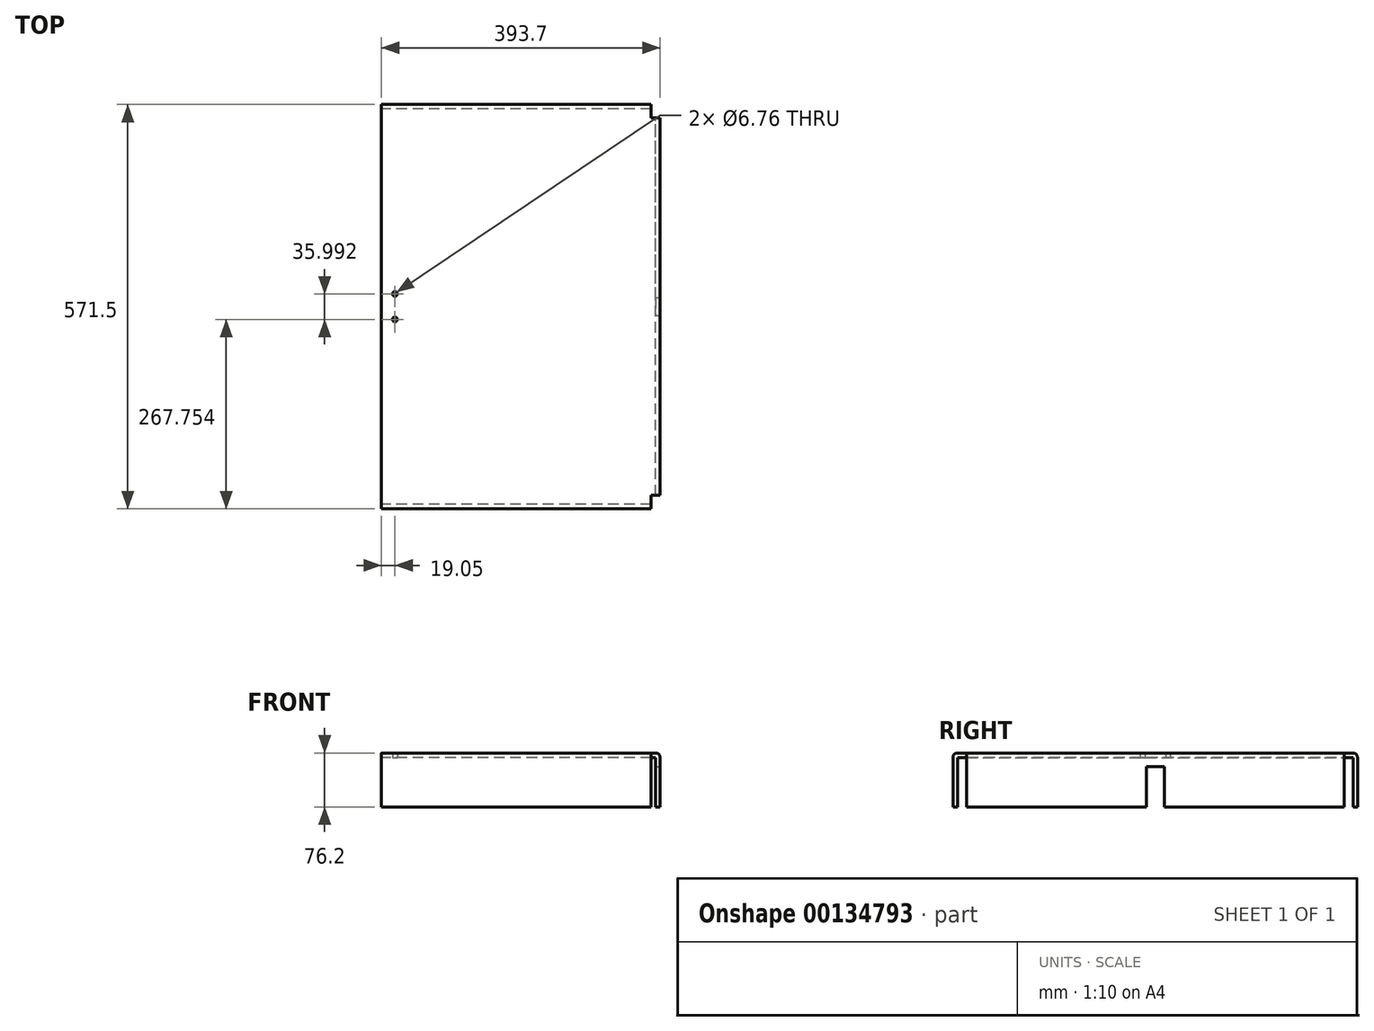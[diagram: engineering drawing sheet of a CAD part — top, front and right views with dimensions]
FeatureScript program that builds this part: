
annotation { "Feature Type Name" : "Feature", "Feature Type Description" : "" }
export const myFeature = defineFeature(function(context is Context, id is Id, definition is map)
    precondition{}
    {
        {
            var Q0;
            Q0=qCreatedBy(makeId("Top.planeOp"),FACE);
            var sketch = newSketch(context, id + "F0", { "sketchPlane" : qUnion([Q0])});
            skLineSegment(sketch, "E0.bottom", {"start": v(190.5, 279.4) * mm, "end": v(-190.5, 279.4) * mm});
            skLineSegment(sketch, "E0.top", {"start": v(190.5, -279.4) * mm, "end": v(-190.5, -279.4) * mm});
            skLineSegment(sketch, "E0.left", {"start": v(190.5, 279.4) * mm, "end": v(190.5, -279.4) * mm});
            skLineSegment(sketch, "E0.right", {"start": v(-190.5, 279.4) * mm, "end": v(-190.5, -279.4) * mm});
            skPoint(sketch, "E0.middle", {"position": v(0, 0) * mm});
            skSolve(sketch);
        }
        {
            var Q0;
            Q0=makeQuery(id+"F0.imprint","IMPRINT",FACE,{"disambiguationData":[TD([[makeQuery(id+"F0.imprint","IMPRINT",EDGE,{"derivedFrom":sQuery(id+"F0.wireOp",EDGE,"E0.bottom")}),1.0]])]});
            extrude(context, id + "F1", {"entities" : qUnion([Q0]), "depth" : 6.35 * mm});
        }
        {
            var Q0;
            Q0=makeQuery(id+"F1.opExtrude","CAP_FACE",FACE,{"disambiguationData":[OSD([sQuery(id+"F0.wireOp",EDGE,"E0.bottom"),sQuery(id+"F0.wireOp",EDGE,"E0.top"),sQuery(id+"F0.wireOp",EDGE,"E0.left"),sQuery(id+"F0.wireOp",EDGE,"E0.right")])],"isStart":false});
            var sketch = newSketch(context, id + "F2", { "sketchPlane" : qUnion([Q0])});
            skLineSegment(sketch, "E1.bottom", {"start": v(190.5, 279.4) * mm, "end": v(-190.5, 279.4) * mm});
            skLineSegment(sketch, "E1.top", {"start": v(190.5, 285.75) * mm, "end": v(-190.5, 285.75) * mm});
            skLineSegment(sketch, "E1.left", {"start": v(190.5, 279.4) * mm, "end": v(190.5, 285.75) * mm});
            skLineSegment(sketch, "E1.right", {"start": v(-190.5, 279.4) * mm, "end": v(-190.5, 285.75) * mm});
            skLineSegment(sketch, "E2.bottom", {"start": v(-190.5, -279.4) * mm, "end": v(190.5, -279.4) * mm});
            skLineSegment(sketch, "E2.top", {"start": v(-190.5, -285.75) * mm, "end": v(190.5, -285.75) * mm});
            skLineSegment(sketch, "E2.left", {"start": v(-190.5, -279.4) * mm, "end": v(-190.5, -285.75) * mm});
            skLineSegment(sketch, "E2.right", {"start": v(190.5, -279.4) * mm, "end": v(190.5, -285.75) * mm});
            skLineSegment(sketch, "E3.bottom", {"start": v(-190.5, -279.4) * mm, "end": v(-196.85, -279.4) * mm});
            skLineSegment(sketch, "E3.top", {"start": v(-190.5, 279.4) * mm, "end": v(-196.85, 279.4) * mm});
            skLineSegment(sketch, "E3.left", {"start": v(-190.5, -279.4) * mm, "end": v(-190.5, 279.4) * mm});
            skLineSegment(sketch, "E3.right", {"start": v(-196.85, -279.4) * mm, "end": v(-196.85, 279.4) * mm});
            skSolve(sketch);
        }
        {
            var Q0;
            Q0=makeQuery(id+"F2.imprint","IMPRINT",FACE,{"disambiguationData":[TD([[makeQuery(id+"F2.imprint","IMPRINT",EDGE,{"derivedFrom":sQuery(id+"F2.wireOp",EDGE,"E2.bottom")}),1.0]])]});
            var Q1;
            Q1=makeQuery(id+"F2.imprint","IMPRINT",FACE,{"disambiguationData":[TD([[makeQuery(id+"F2.imprint","IMPRINT",EDGE,{"derivedFrom":sQuery(id+"F2.wireOp",EDGE,"E1.bottom")}),-1.0]])]});
            extrude(context, id + "F3", {"entities" : qUnion([Q0, Q1]), "operationType" : NewBodyOperationType.ADD, "oppositeDirection" : true, "depth" : 76.2 * mm});
        }
        {
            var Q0;
            Q0=makeQuery(id+"F3.boolean.opBoolean","MERGE",FACE,{"derivedFrom":[makeQuery(id+"F1.opExtrude","CAP_FACE",FACE,{"disambiguationData":[OSD([sQuery(id+"F0.wireOp",EDGE,"E0.bottom"),sQuery(id+"F0.wireOp",EDGE,"E0.top"),sQuery(id+"F0.wireOp",EDGE,"E0.left"),sQuery(id+"F0.wireOp",EDGE,"E0.right")])],"isStart":false}),makeQuery(id+"F3.opExtrude","CAP_FACE",FACE,{"disambiguationData":[OSD([sQuery(id+"F2.wireOp",EDGE,"E1.bottom"),sQuery(id+"F2.wireOp",EDGE,"E1.top"),sQuery(id+"F2.wireOp",EDGE,"E1.left"),sQuery(id+"F2.wireOp",EDGE,"E1.right")])],"isStart":true}),makeQuery(id+"F3.opExtrude","CAP_FACE",FACE,{"disambiguationData":[OSD([sQuery(id+"F2.wireOp",EDGE,"E2.bottom"),sQuery(id+"F2.wireOp",EDGE,"E2.top"),sQuery(id+"F2.wireOp",EDGE,"E2.left"),sQuery(id+"F2.wireOp",EDGE,"E2.right")])],"isStart":true})]});
            var sketch = newSketch(context, id + "F4", { "sketchPlane" : qUnion([Q0])});
            skLineSegment(sketch, "E4.bottom", {"start": v(190.5, -266.7) * mm, "end": v(203.2, -266.7) * mm});
            skLineSegment(sketch, "E4.top", {"start": v(190.5, 266.7) * mm, "end": v(203.2, 266.7) * mm});
            skLineSegment(sketch, "E4.left", {"start": v(190.5, -266.7) * mm, "end": v(190.5, 266.7) * mm});
            skLineSegment(sketch, "E4.right", {"start": v(203.2, -266.7) * mm, "end": v(203.2, 266.7) * mm});
            skSolve(sketch);
        }
        {
            var Q0;
            Q0=makeQuery(id+"F4.imprint","IMPRINT",FACE,{"disambiguationData":[TD([[makeQuery(id+"F4.imprint","IMPRINT",EDGE,{"derivedFrom":sQuery(id+"F4.wireOp",EDGE,"E4.bottom")}),1.0]])]});
            extrude(context, id + "F5", {"entities" : qUnion([Q0]), "operationType" : NewBodyOperationType.ADD, "oppositeDirection" : true, "depth" : 6.35 * mm});
        }
        {
            var Q0;
            Q0=makeQuery(id+"F5.boolean.opBoolean","MERGE",FACE,{"derivedFrom":[makeQuery(id+"F1.opExtrude","CAP_FACE",FACE,{"disambiguationData":[OSD([sQuery(id+"F0.wireOp",EDGE,"E0.bottom"),sQuery(id+"F0.wireOp",EDGE,"E0.top"),sQuery(id+"F0.wireOp",EDGE,"E0.left"),sQuery(id+"F0.wireOp",EDGE,"E0.right")])],"isStart":true}),makeQuery(id+"F5.opExtrude","CAP_FACE",FACE,{"disambiguationData":[OSD([sQuery(id+"F4.wireOp",EDGE,"E4.bottom"),sQuery(id+"F4.wireOp",EDGE,"E4.top"),sQuery(id+"F4.wireOp",EDGE,"E4.left"),sQuery(id+"F4.wireOp",EDGE,"E4.right")])],"isStart":false})]});
            var sketch = newSketch(context, id + "F6", { "sketchPlane" : qUnion([Q0])});
            skLineSegment(sketch, "E5.bottom", {"start": v(203.2, 266.7) * mm, "end": v(196.85, 266.7) * mm});
            skLineSegment(sketch, "E5.top", {"start": v(203.2, -266.7) * mm, "end": v(196.85, -266.7) * mm});
            skLineSegment(sketch, "E5.left", {"start": v(203.2, 266.7) * mm, "end": v(203.2, -266.7) * mm});
            skLineSegment(sketch, "E5.right", {"start": v(196.85, 266.7) * mm, "end": v(196.85, -266.7) * mm});
            skSolve(sketch);
        }
        {
            var Q0;
            Q0=makeQuery(id+"F6.imprint","IMPRINT",FACE,{"disambiguationData":[TD([[makeQuery(id+"F6.imprint","IMPRINT",EDGE,{"derivedFrom":sQuery(id+"F6.wireOp",EDGE,"E5.bottom")}),-1.0]])]});
            extrude(context, id + "F7", {"entities" : qUnion([Q0]), "operationType" : NewBodyOperationType.ADD, "depth" : 69.85 * mm});
        }
        {
            var Q0;
            Q0=makeQuery(id+"F7.boolean.opBoolean","MERGE",FACE,{"derivedFrom":[makeQuery(id+"F5.opExtrude","SWEPT_FACE",FACE,{"disambiguationData":[OSD([sQuery(id+"F4.wireOp",EDGE,"E4.right")])]}),makeQuery(id+"F7.opExtrude","SWEPT_FACE",FACE,{"disambiguationData":[OSD([sQuery(id+"F6.wireOp",EDGE,"E5.left")])]})]});
            var sketch = newSketch(context, id + "F8", { "sketchPlane" : qUnion([Q0])});
            skLineSegment(sketch, "E6.top", {"start": v(-12.7, -69.85) * mm, "end": v(12.7, -69.85) * mm});
            skLineSegment(sketch, "E7", {"start": v(-12.7, -69.85) * mm, "end": v(-12.7, -12.7) * mm});
            skLineSegment(sketch, "E8", {"start": v(12.7, -69.85) * mm, "end": v(12.7, -12.7) * mm});
            skLineSegment(sketch, "E9", {"start": v(12.7, -12.7) * mm, "end": v(-12.7, -12.7) * mm});
            skSolve(sketch);
        }
        {
            var Q0;
            Q0=makeQuery(id+"F8.imprint","IMPRINT",FACE,{"disambiguationData":[TD([[makeQuery(id+"F8.imprint","IMPRINT",EDGE,{"derivedFrom":sQuery(id+"F8.wireOp",EDGE,"E6.top")}),1.0]])]});
            extrude(context, id + "F9", {"entities" : qUnion([Q0]), "operationType" : NewBodyOperationType.REMOVE, "endBound" : BoundingType.THROUGH_ALL, "oppositeDirection" : true, "depth" : 25.4 * mm});
        }
        {
            var Q0;
            Q0=makeQuery(id+"F3.opExtrude","CAP_EDGE",EDGE,{"disambiguationData":[OSD([sQuery(id+"F2.wireOp",EDGE,"E1.top")])],"isStart":true});
            var Q1;
            Q1=makeQuery(id+"F3.opExtrude","CAP_EDGE",EDGE,{"disambiguationData":[OSD([sQuery(id+"F2.wireOp",EDGE,"E2.top")])],"isStart":true});
            var Q2;
            Q2=makeQuery(id+"F5.opExtrude","CAP_EDGE",EDGE,{"disambiguationData":[OSD([sQuery(id+"F4.wireOp",EDGE,"E4.right")])],"isStart":true});
            var Q3;
            Q3=makeQuery(id+"F1.opExtrude","CAP_EDGE",EDGE,{"disambiguationData":[OSD([sQuery(id+"F0.wireOp",EDGE,"E0.top")])],"isStart":true});
            var Q4;
            Q4=makeQuery(id+"F7.opExtrude","CAP_EDGE",EDGE,{"disambiguationData":[OSD([sQuery(id+"F6.wireOp",EDGE,"E5.right")])],"isStart":true});
            var Q5;
            Q5=makeQuery(id+"F1.opExtrude","CAP_EDGE",EDGE,{"disambiguationData":[OSD([sQuery(id+"F0.wireOp",EDGE,"E0.bottom")])],"isStart":true});
            fillet(context, id + "F10", {"entities" : qUnion([Q0, Q1, Q2, Q3, Q4, Q5]), "radius" : 6.35 * mm, "tangentPropagation" : true, "allowEdgeOverflow" : false});
        }
        {
            var Q0;
            Q0=makeQuery(id+"F5.boolean.opBoolean","MERGE",FACE,{"derivedFrom":[makeQuery(id+"F1.opExtrude","CAP_FACE",FACE,{"disambiguationData":[OSD([sQuery(id+"F0.wireOp",EDGE,"E0.bottom"),sQuery(id+"F0.wireOp",EDGE,"E0.top"),sQuery(id+"F0.wireOp",EDGE,"E0.left"),sQuery(id+"F0.wireOp",EDGE,"E0.right")])],"isStart":true}),makeQuery(id+"F5.opExtrude","CAP_FACE",FACE,{"disambiguationData":[OSD([sQuery(id+"F4.wireOp",EDGE,"E4.bottom"),sQuery(id+"F4.wireOp",EDGE,"E4.top"),sQuery(id+"F4.wireOp",EDGE,"E4.left"),sQuery(id+"F4.wireOp",EDGE,"E4.right")])],"isStart":false})]});
            var sketch = newSketch(context, id + "F11", { "sketchPlane" : qUnion([Q0])});
            skPoint(sketch, "E10", {"position": v(-171.45, 18) * mm});
            skPoint(sketch, "E11", {"position": v(-171.45, -18) * mm});
            skSolve(sketch);
        }
        {
            var Q0;
            Q0=sQuery(id+"F11.wireOp",VERTEX,"E10");
            var Q1;
            Q1=sQuery(id+"F11.wireOp",VERTEX,"E11");
            var Q2;
            Q2=makeQuery(id+"F1.opExtrude","SWEPT_BODY",BODY,{"disambiguationData":[OSD([sQuery(id+"F0.wireOp",EDGE,"E0.bottom"),sQuery(id+"F0.wireOp",EDGE,"E0.top"),sQuery(id+"F0.wireOp",EDGE,"E0.left"),sQuery(id+"F0.wireOp",EDGE,"E0.right")])]});
            hole(context, id + "F12", {"style" : HoleStyle.SIMPLE, "endStyle" : HoleEndStyle.THROUGH, "standardTappedOrClearance" : lookupTablePath({ "standard" : "ANSI", "fit" : "Normal (ASME)", "size" : "1/4", "type" : "Clearance" }), "standardBlindInLast" : lookupTablePath({ "fit" : "Free", "standard" : "ANSI", "size" : "1/4", "type" : "Clearance" }), "holeDiameter" : 6.76 * mm, "locations" : qUnion([Q0, Q1]), "scope" : qUnion([Q2]), "isTappedThrough" : true});
        }
    });
